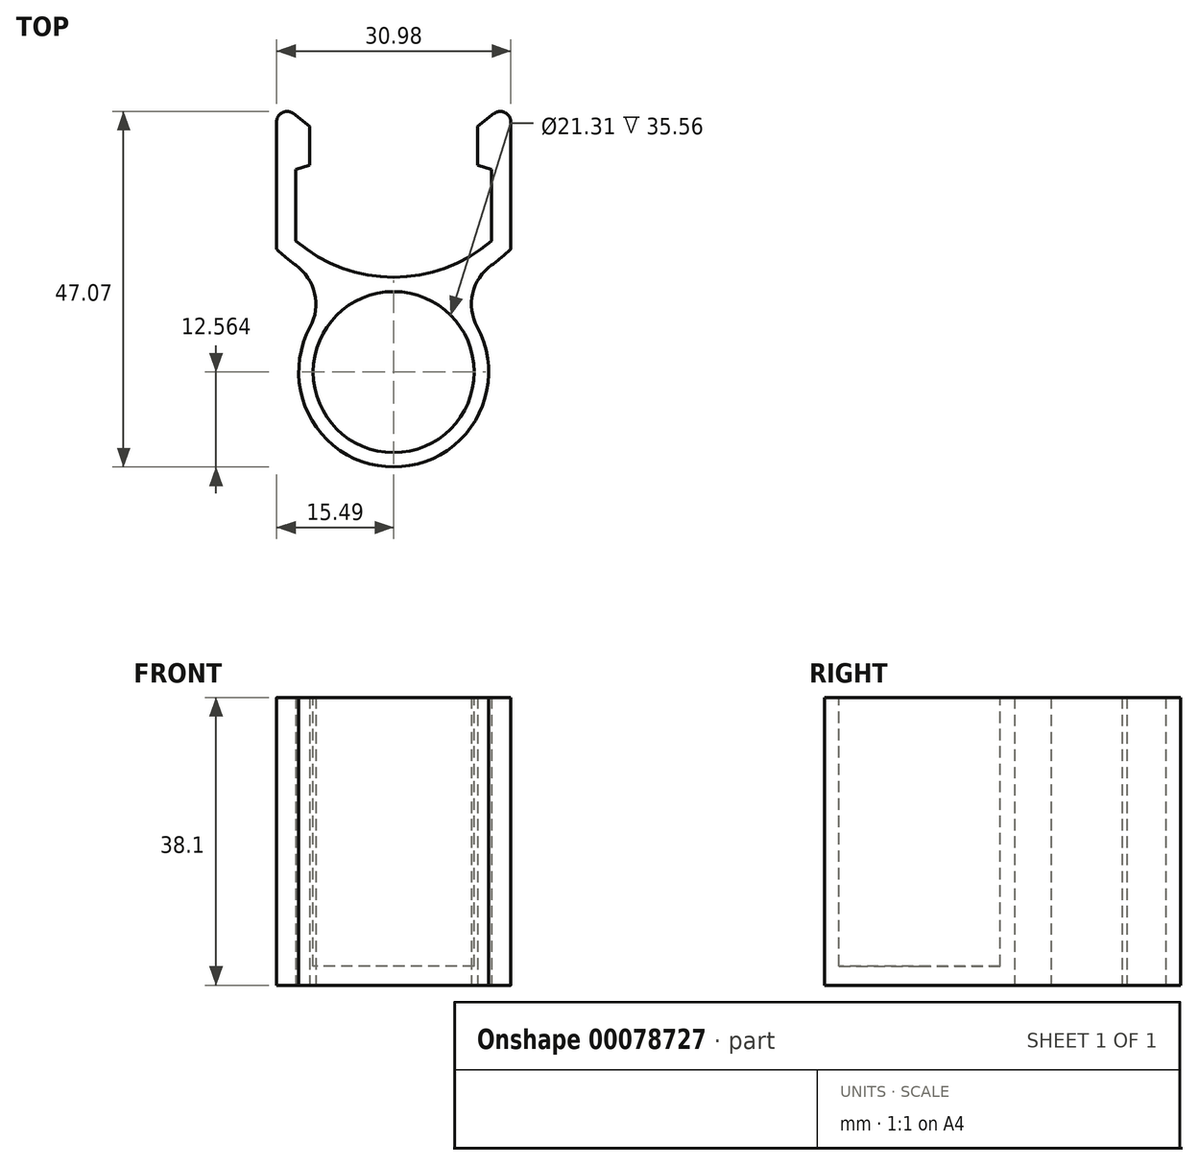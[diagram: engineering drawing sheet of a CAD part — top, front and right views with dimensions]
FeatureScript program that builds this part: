
annotation { "Feature Type Name" : "Feature", "Feature Type Description" : "" }
export const myFeature = defineFeature(function(context is Context, id is Id, definition is map)
    precondition{}
    {
        {
            var Q0;
            Q0=qCreatedBy(makeId("Top.planeOp"),FACE);
            var sketch = newSketch(context, id + "F0", { "sketchPlane" : qUnion([Q0])});
            skLineSegment(sketch, "E0", {"start": v(0, 0) * mm, "end": v(0, -12.7) * mm, "construction": true});
            skLineSegment(sketch, "E1", {"start": v(0, 0) * mm, "end": v(-12.62, 0) * mm, "construction": true});
            skLineSegment(sketch, "E2", {"start": v(0, -4.57) * mm, "end": v(-3.17, -4.57) * mm});
            skLineSegment(sketch, "E3", {"start": v(-3.17, -4.57) * mm, "end": v(-3.17, -12.7) * mm});
            skLineSegment(sketch, "E4", {"start": v(-3.17, -12.7) * mm, "end": v(-12.7, -12.7) * mm});
            skLineSegment(sketch, "E5", {"start": v(-12.7, -12.7) * mm, "end": v(-12.7, -3.18) * mm});
            skLineSegment(sketch, "E6", {"start": v(-12.7, -3.18) * mm, "end": v(-4.57, -3.18) * mm});
            skLineSegment(sketch, "E7", {"start": v(-4.57, -3.18) * mm, "end": v(-4.57, 0) * mm});
            skLineSegment(sketch, "E8.MirrorCS", {"start": v(0, -4.57) * mm, "end": v(3.17, -4.57) * mm});
            skLineSegment(sketch, "E9.MirrorCS", {"start": v(3.18, -4.57) * mm, "end": v(3.18, -12.7) * mm});
            skLineSegment(sketch, "E10.MirrorCS", {"start": v(3.18, -12.7) * mm, "end": v(12.7, -12.7) * mm});
            skLineSegment(sketch, "E11.MirrorCS", {"start": v(12.7, -12.7) * mm, "end": v(12.7, -3.18) * mm});
            skLineSegment(sketch, "E12.MirrorCS", {"start": v(4.57, -3.17) * mm, "end": v(4.57, 0) * mm});
            skLineSegment(sketch, "E13.MirrorCS", {"start": v(12.7, -3.18) * mm, "end": v(4.57, -3.18) * mm});
            skLineSegment(sketch, "E14.MirrorCS", {"start": v(0, 0) * mm, "end": v(12.62, 0) * mm, "construction": true});
            skLineSegment(sketch, "E15.MirrorCS", {"start": v(3.17, 12.7) * mm, "end": v(12.7, 12.7) * mm});
            skLineSegment(sketch, "E16.MirrorCS", {"start": v(-3.18, 12.7) * mm, "end": v(-12.7, 12.7) * mm});
            skLineSegment(sketch, "E17.MirrorCS", {"start": v(0, 4.57) * mm, "end": v(-3.17, 4.57) * mm});
            skLineSegment(sketch, "E18.MirrorCS", {"start": v(0, 4.57) * mm, "end": v(3.17, 4.57) * mm});
            skLineSegment(sketch, "E19.MirrorCS", {"start": v(12.7, 3.18) * mm, "end": v(4.57, 3.18) * mm});
            skLineSegment(sketch, "E20.MirrorCS", {"start": v(-12.7, 3.17) * mm, "end": v(-4.57, 3.18) * mm});
            skLineSegment(sketch, "E21.MirrorCS", {"start": v(12.7, 12.7) * mm, "end": v(12.7, 3.18) * mm});
            skLineSegment(sketch, "E22.MirrorCS", {"start": v(3.18, 4.57) * mm, "end": v(3.18, 12.7) * mm});
            skLineSegment(sketch, "E23.MirrorCS", {"start": v(-12.7, 12.7) * mm, "end": v(-12.7, 3.18) * mm});
            skLineSegment(sketch, "E24.MirrorCS", {"start": v(-3.17, 4.57) * mm, "end": v(-3.17, 12.7) * mm});
            skLineSegment(sketch, "E25.MirrorCS", {"start": v(4.57, 3.18) * mm, "end": v(4.57, 0) * mm});
            skLineSegment(sketch, "E26.MirrorCS", {"start": v(-4.57, 3.18) * mm, "end": v(-4.57, 0) * mm});
            skSolve(sketch);
        }
        {
            var Q0;
            Q0=qCreatedBy(makeId("Top.planeOp"),FACE);
            var sketch = newSketch(context, id + "F1", { "sketchPlane" : qUnion([Q0])});
            skLineSegment(sketch, "E27", {"start": v(0, 0) * mm, "end": v(0, -35.56) * mm, "construction": true});
            skLineSegment(sketch, "E28", {"start": v(-11.11, 2.23) * mm, "end": v(-11.11, -2.92) * mm});
            skLineSegment(sketch, "E29", {"start": v(-11.11, -2.92) * mm, "end": v(-12.95, -3.52) * mm});
            skLineSegment(sketch, "E30", {"start": v(-12.95, -3.52) * mm, "end": v(-12.95, -12.95) * mm});
            skLineSegment(sketch, "E31.MirrorCS", {"start": v(12.95, -3.52) * mm, "end": v(12.95, -12.95) * mm});
            skLineSegment(sketch, "E32.MirrorCS", {"start": v(11.11, 2.23) * mm, "end": v(11.11, -2.92) * mm});
            skLineSegment(sketch, "E33.MirrorCS", {"start": v(11.11, -2.92) * mm, "end": v(12.95, -3.52) * mm});
            skArc(sketch, "E34", {"start": v(-12.95, -12.95) * mm, "mid": v(-6.91, -16.53) * mm, "end": v(0, -17.78) * mm});
            skArc(sketch, "E35.MirrorCS", {"start": v(12.95, -12.95) * mm, "mid": v(6.91, -16.53) * mm, "end": v(0, -17.78) * mm});
            skCircle(sketch, "E36", {"center": v(0, -30.34) * mm, "radius": 10.02 * mm, "construction": true});
            skArc(sketch, "E37.0", {"start": v(-15.38, -14.19) * mm, "mid": v(-14.2, -15.22) * mm, "end": v(-12.96, -16.18) * mm});
            skLineSegment(sketch, "E37.1", {"start": v(-15.5, 2.79) * mm, "end": v(-15.5, -13.91) * mm});
            skArc(sketch, "E38.0", {"start": v(-11.05, -24.37) * mm, "mid": v(0, -42.9) * mm, "end": v(11.05, -24.37) * mm});
            skArc(sketch, "E39.MirrorCS", {"start": v(15.38, -14.19) * mm, "mid": v(14.2, -15.22) * mm, "end": v(12.96, -16.18) * mm});
            skLineSegment(sketch, "E40.MirrorCS", {"start": v(15.5, 2.79) * mm, "end": v(15.5, -13.91) * mm});
            skPoint(sketch, "E41.visualSharp", {"position": v(-6.23, -19.43) * mm});
            skArc(sketch, "E41.filletArc", {"start": v(-11.05, -24.37) * mm, "mid": v(-10.45, -19.91) * mm, "end": v(-12.96, -16.18) * mm});
            skPoint(sketch, "E42.visualSharp", {"position": v(6.23, -19.43) * mm});
            skArc(sketch, "E42.filletArc", {"start": v(12.96, -16.18) * mm, "mid": v(10.45, -19.91) * mm, "end": v(11.05, -24.37) * mm});
            skPoint(sketch, "E43.visualSharp", {"position": v(15.5, -14.07) * mm});
            skArc(sketch, "E43.filletArc", {"start": v(15.38, -14.19) * mm, "mid": v(15.46, -14.06) * mm, "end": v(15.5, -13.91) * mm});
            skPoint(sketch, "E44.visualSharp", {"position": v(-15.5, -14.07) * mm});
            skArc(sketch, "E44.filletArc", {"start": v(-15.5, -13.91) * mm, "mid": v(-15.46, -14.06) * mm, "end": v(-15.38, -14.19) * mm});
            skLineSegment(sketch, "E45", {"start": v(-11.11, 2.23) * mm, "end": v(-13.27, 3.89) * mm});
            skArc(sketch, "E46", {"start": v(-13.27, 3.89) * mm, "mid": v(-14.72, 4.03) * mm, "end": v(-15.5, 2.79) * mm});
            skLineSegment(sketch, "E47.MirrorCS", {"start": v(11.11, 2.23) * mm, "end": v(13.27, 3.89) * mm});
            skArc(sketch, "E48.MirrorCS", {"start": v(13.27, 3.89) * mm, "mid": v(14.72, 4.03) * mm, "end": v(15.5, 2.79) * mm});
            skSolve(sketch);
        }
        {
            var Q0;
            Q0 = qSketchRegion(id + "F1", true);
            extrude(context, id + "F2", {"entities" : qUnion([Q0]), "depth" : 38.1 * mm});
        }
        {
            var Q0;
            Q0=makeQuery(id+"F2.opExtrude","CAP_FACE",FACE,{"disambiguationData":[OSD([sQuery(id+"F1.wireOp",EDGE,"E28"),sQuery(id+"F1.wireOp",EDGE,"E29"),sQuery(id+"F1.wireOp",EDGE,"E30"),sQuery(id+"F1.wireOp",EDGE,"E31.MirrorCS"),sQuery(id+"F1.wireOp",EDGE,"E32.MirrorCS"),sQuery(id+"F1.wireOp",EDGE,"E33.MirrorCS"),sQuery(id+"F1.wireOp",EDGE,"E34"),sQuery(id+"F1.wireOp",EDGE,"E35.MirrorCS"),sQuery(id+"F1.wireOp",EDGE,"l96RwAy3-4KYR-Wzle-W6J1-3fBcWALWH1dM"),sQuery(id+"F1.wireOp",EDGE,"mvamLMCA-wUrf-2y6I-UD9c-N1kgiWEsCUB4"),sQuery(id+"F1.wireOp",EDGE,"E37.0"),sQuery(id+"F1.wireOp",EDGE,"E37.1"),sQuery(id+"F1.wireOp",EDGE,"E38.0"),sQuery(id+"F1.wireOp",EDGE,"E39.MirrorCS"),sQuery(id+"F1.wireOp",EDGE,"E40.MirrorCS"),sQuery(id+"F1.wireOp",EDGE,"1c6ecec6-655d-4a65-bb61-8720271be6872.MirrorCS"),sQuery(id+"F1.wireOp",EDGE,"1c6ecec6-655d-4a65-bb61-8720271be6873.MirrorCS"),sQuery(id+"F1.wireOp",EDGE,"E41.filletArc"),sQuery(id+"F1.wireOp",EDGE,"E42.filletArc"),sQuery(id+"F1.wireOp",EDGE,"E43.filletArc"),sQuery(id+"F1.wireOp",EDGE,"E44.filletArc"),sQuery(id+"F1.wireOp",EDGE,"4b17010a-e1b8-40fd-a6c5-b50b13651ef8.filletArc"),sQuery(id+"F1.wireOp",EDGE,"97084cd8-e749-434a-9b29-a5b8ae9078f6.filletArc"),sQuery(id+"F1.wireOp",EDGE,"8db9bc3c-7e0b-494a-a7e8-4776762aa71b.filletArc"),sQuery(id+"F1.wireOp",EDGE,"d2d11487-7237-49c0-9a23-f76624aa791c.filletArc"),sQuery(id+"F1.wireOp",EDGE,"d0d56a40-d7e0-45e8-8c97-8842f7ba5fbe.filletArc"),sQuery(id+"F1.wireOp",EDGE,"5d8a1d59-dd57-4b31-8e3e-cadda728cfc3.filletArc")])],"isStart":false});
            var sketch = newSketch(context, id + "F3", { "sketchPlane" : qUnion([Q0])});
            skCircle(sketch, "E49.0", {"center": v(0, -30.34) * mm, "radius": 10.66 * mm});
            skSolve(sketch);
        }
        {
            var Q0;
            Q0 = qSketchRegion(id + "F3", true);
            extrude(context, id + "F4", {"entities" : qUnion([Q0]), "operationType" : NewBodyOperationType.REMOVE, "oppositeDirection" : true, "depth" : 35.56 * mm});
        }
    });
